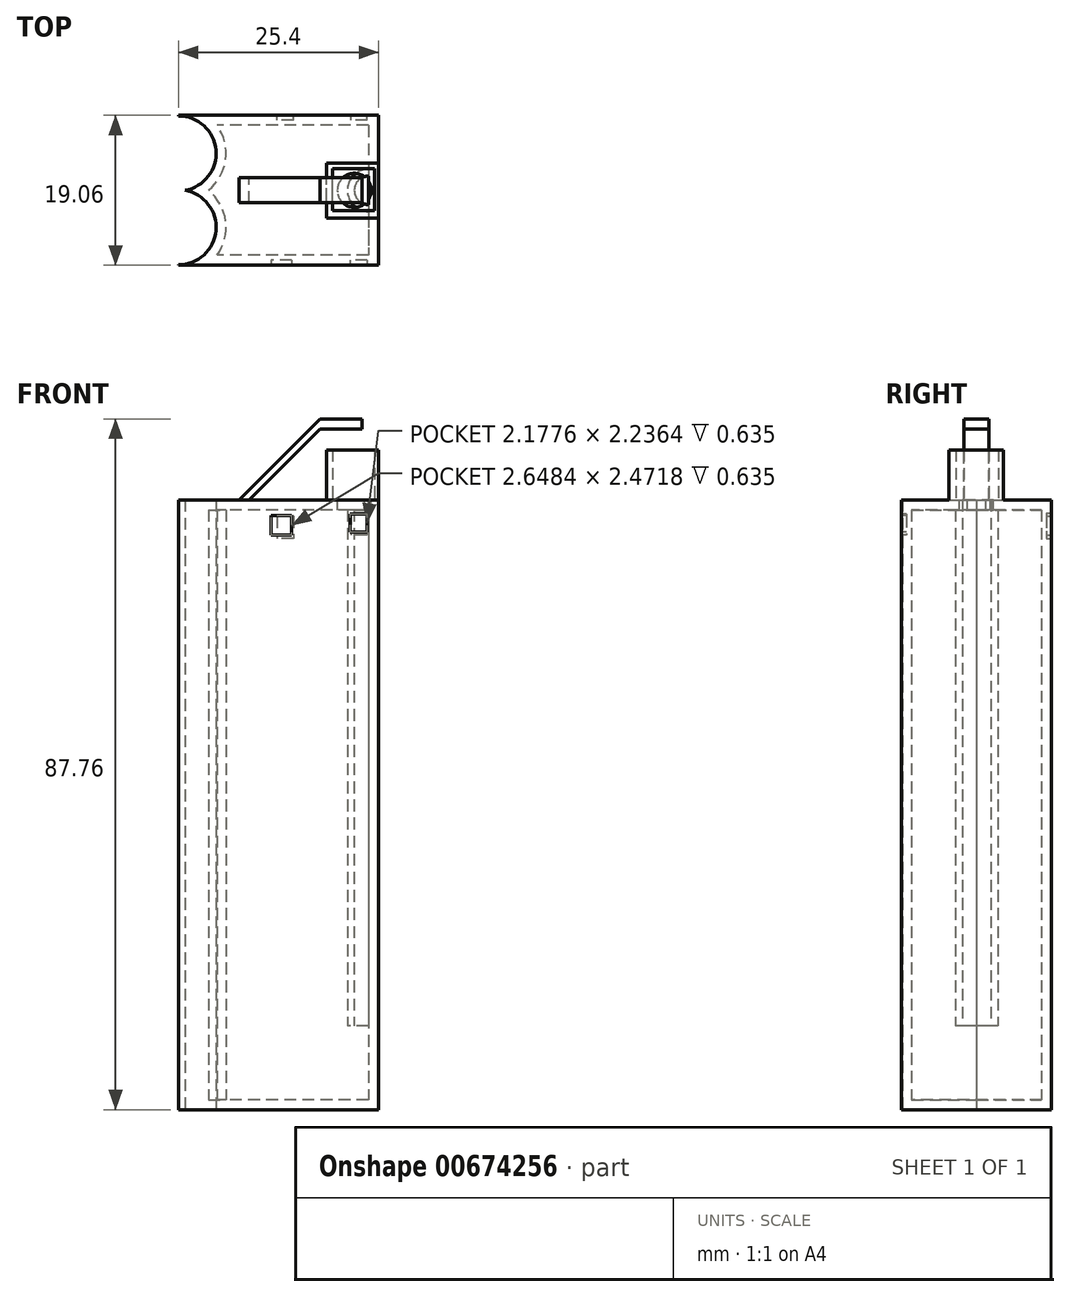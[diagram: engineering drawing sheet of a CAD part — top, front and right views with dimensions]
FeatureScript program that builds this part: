
annotation { "Feature Type Name" : "Feature", "Feature Type Description" : "" }
export const myFeature = defineFeature(function(context is Context, id is Id, definition is map)
    precondition{}
    {
        {
            var Q0;
            Q0=qCreatedBy(makeId("Top.planeOp"),FACE);
            var sketch = newSketch(context, id + "F0", { "sketchPlane" : qUnion([Q0])});
            skLineSegment(sketch, "E0.bottom", {"start": v(0, 9.53) * mm, "end": v(-25.4, 9.53) * mm});
            skLineSegment(sketch, "E0.top", {"start": v(0, -9.52) * mm, "end": v(-25.4, -9.53) * mm});
            skLineSegment(sketch, "E0.left", {"start": v(0, 9.53) * mm, "end": v(0, -9.52) * mm});
            skLineSegment(sketch, "E0.right", {"start": v(-25.4, 9.53) * mm, "end": v(-25.4, -9.53) * mm});
            skLineSegment(sketch, "E1", {"start": v(0, 0) * mm, "end": v(-25.4, 0) * mm, "construction": true});
            skCircle(sketch, "E2", {"center": v(-25.4, 4.7) * mm, "radius": 4.76 * mm});
            skCircle(sketch, "E3.MirrorC", {"center": v(-25.4, -4.7) * mm, "radius": 4.76 * mm});
            skSolve(sketch);
        }
        {
            var Q0;
            {var subQ1=sQuery(id+"F0.wireOp",EDGE,"E0.bottom");Q0=makeQuery(id+"F0.imprint","IMPRINT",FACE,{"disambiguationData":[TD([[makeQuery(id+"F0.imprint","IMPRINT",EDGE,{"derivedFrom":subQ1}),1.0]])]});}
            extrude(context, id + "F1", {"entities" : qUnion([Q0]), "depth" : 76.2 * mm, "offsetDistance" : 25.4 * mm});
        }
        {
            var Q0;
            Q0=makeQuery(id+"F1.opExtrude","CAP_FACE",FACE,{"disambiguationData":[OSD([sQuery(id+"F0.wireOp",EDGE,"E0.bottom"),sQuery(id+"F0.wireOp",EDGE,"E0.top"),sQuery(id+"F0.wireOp",EDGE,"E0.left"),sQuery(id+"F0.wireOp",EDGE,"E0.right"),sQuery(id+"F0.wireOp",EDGE,"E2"),sQuery(id+"F0.wireOp",EDGE,"E3.MirrorC")])],"isStart":false});
            shell(context, id + "F2", {"entities" : qUnion([Q0]), "thickness" : 1.27 * mm});
        }
        {
            var Q0;
            Q0=qCreatedBy(makeId("Top.planeOp"),FACE);
            var sketch = newSketch(context, id + "F3", { "sketchPlane" : qUnion([Q0])});
            skLineSegment(sketch, "E4.0", {"start": v(-1.27, 8.26) * mm, "end": v(-1.27, -8.25) * mm});
            skArc(sketch, "E5", {"start": v(-1.27, 1.81) * mm, "mid": v(-3.08, 0) * mm, "end": v(-1.27, -1.81) * mm});
            skArc(sketch, "E6", {"start": v(-1.27, 2.7) * mm, "mid": v(-3.96, 0) * mm, "end": v(-1.27, -2.7) * mm});
            skLineSegment(sketch, "E7", {"start": v(-1.27, 2.7) * mm, "end": v(-1.27, 1.81) * mm});
            skLineSegment(sketch, "E8", {"start": v(-1.27, -1.81) * mm, "end": v(-1.27, -2.7) * mm});
            skSolve(sketch);
        }
        {
            var Q0;
            Q0=makeQuery(id+"F3.imprint","IMPRINT",FACE,{"disambiguationData":[TD([[makeQuery(id+"F3.imprint","IMPRINT",EDGE,{"derivedFrom":sQuery(id+"F3.wireOp",EDGE,"E5")}),-1.0]])]});
            extrude(context, id + "F4", {"entities" : qUnion([Q0]), "operationType" : NewBodyOperationType.ADD, "depth" : 76.2 * mm, "offsetDistance" : 25.4 * mm});
        }
        {
            var Q0;
            {var subQ1=sQuery(id+"F0.wireOp",EDGE,"E0.top");var subQ5=sQuery(id+"F0.wireOp",EDGE,"E0.left");Q0=makeQuery(id+"F4.boolean.opBoolean","SPLIT",FACE,{"disambiguationData":[TD([makeQuery(id+"F2.opShell","OFFSET_FACE",FACE,{"disambiguationData":[OSD([subQ1])]})])],"derivedFrom":makeQuery(id+"F2.opShell","OFFSET_FACE",FACE,{"disambiguationData":[OSD([subQ5])]})});}
            var sketch = newSketch(context, id + "F5", { "sketchPlane" : qUnion([Q0])});
            skLineSegment(sketch, "E9.0", {"start": v(2.7, 1.27) * mm, "end": v(-2.7, 1.27) * mm});
            skLineSegment(sketch, "E10.bottom", {"start": v(-3.44, 1.27) * mm, "end": v(2.7, 1.27) * mm});
            skLineSegment(sketch, "E10.top", {"start": v(-3.44, 10.63) * mm, "end": v(2.7, 10.63) * mm});
            skLineSegment(sketch, "E10.left", {"start": v(-3.44, 1.27) * mm, "end": v(-3.44, 10.63) * mm});
            skLineSegment(sketch, "E10.right", {"start": v(2.7, 1.27) * mm, "end": v(2.7, 10.63) * mm});
            skSolve(sketch);
        }
        {
            var Q0;
            Q0=makeQuery(id+"F5.imprint","IMPRINT",FACE,{"disambiguationData":[TD([[makeQuery(id+"F5.imprint","IMPRINT",EDGE,{"derivedFrom":sQuery(id+"F5.wireOp",EDGE,"E10.top")}),-1.0]])]});
            extrude(context, id + "F6", {"entities" : qUnion([Q0]), "operationType" : NewBodyOperationType.REMOVE, "depth" : 12.7 * mm, "offsetDistance" : 25.4 * mm});
        }
        {
            var Q0;
            Q0=makeQuery(id+"F4.boolean.opBoolean","MERGE",FACE,{"derivedFrom":[makeQuery(id+"F1.opExtrude","CAP_FACE",FACE,{"disambiguationData":[OSD([sQuery(id+"F0.wireOp",EDGE,"E0.bottom"),sQuery(id+"F0.wireOp",EDGE,"E0.top"),sQuery(id+"F0.wireOp",EDGE,"E0.left"),sQuery(id+"F0.wireOp",EDGE,"E0.right"),sQuery(id+"F0.wireOp",EDGE,"E2"),sQuery(id+"F0.wireOp",EDGE,"E3.MirrorC")])],"isStart":false}),makeQuery(id+"F4.opExtrude","CAP_FACE",FACE,{"disambiguationData":[OSD([sQuery(id+"F3.wireOp",EDGE,"E5"),sQuery(id+"F3.wireOp",EDGE,"E6"),sQuery(id+"F3.wireOp",EDGE,"E7"),sQuery(id+"F3.wireOp",EDGE,"E8")])],"isStart":false})]});
            var sketch = newSketch(context, id + "F7", { "sketchPlane" : qUnion([Q0])});
            skLineSegment(sketch, "E11.0", {"start": v(0, 9.53) * mm, "end": v(-25.4, 9.53) * mm});
            skPoint(sketch, "E12.0", {"position": v(-1.27, 5.47) * mm});
            skLineSegment(sketch, "E13.0", {"start": v(0, 9.53) * mm, "end": v(0, -9.52) * mm});
            skLineSegment(sketch, "E14.0", {"start": v(0, -9.52) * mm, "end": v(-25.4, -9.53) * mm});
            skPoint(sketch, "E15.0", {"position": v(-20.66, -5.1) * mm});
            skArc(sketch, "E16.0", {"start": v(-24.58, 0) * mm, "mid": v(-20.66, -5.1) * mm, "end": v(-25.4, -9.45) * mm});
            skArc(sketch, "E17.0", {"start": v(-24.58, 0) * mm, "mid": v(-20.66, 5.1) * mm, "end": v(-25.4, 9.45) * mm});
            skArc(sketch, "E18.0", {"start": v(-1.27, 1.81) * mm, "mid": v(-3.08, 0) * mm, "end": v(-1.27, -1.81) * mm});
            skLineSegment(sketch, "E19.0", {"start": v(-1.27, 1.81) * mm, "end": v(-1.27, -1.81) * mm});
            skSolve(sketch);
        }
        {
            var Q0;
            Q0=makeQuery(id+"F7.imprint","IMPRINT",FACE,{"disambiguationData":[TD([[makeQuery(id+"F7.imprint","IMPRINT",EDGE,{"derivedFrom":sQuery(id+"F7.wireOp",EDGE,"E11.0")}),1.0]])]});
            var Q1;
            {var subQ4=sQuery(id+"F3.wireOp",EDGE,"E6");Q1=makeQuery(id+"F7.imprint","IMPRINT",FACE,{"disambiguationData":[TD([[makeQuery(id+"F7.imprint","IMPRINT",EDGE,{"derivedFrom":makeQuery(id+"F4.opExtrude","CAP_EDGE",EDGE,{"disambiguationData":[OSD([subQ4])],"isStart":false})}),-1.0]])]});}
            extrude(context, id + "F8", {"entities" : qUnion([Q0, Q1]), "operationType" : NewBodyOperationType.ADD, "depth" : 1.27 * mm, "offsetDistance" : 25.4 * mm});
        }
        {
            var Q0;
            Q0=makeQuery(id+"F8.opExtrude","CAP_FACE",FACE,{"disambiguationData":[OSD([sQuery(id+"F0.wireOp",EDGE,"E0.right"),sQuery(id+"F7.wireOp",EDGE,"E11.0"),sQuery(id+"F7.wireOp",EDGE,"E13.0"),sQuery(id+"F7.wireOp",EDGE,"E14.0"),sQuery(id+"F7.wireOp",EDGE,"E16.0"),sQuery(id+"F7.wireOp",EDGE,"E17.0"),sQuery(id+"F7.wireOp",EDGE,"E18.0"),sQuery(id+"F7.wireOp",EDGE,"E19.0")])],"isStart":false});
            var sketch = newSketch(context, id + "F9", { "sketchPlane" : qUnion([Q0])});
            skCircle(sketch, "E20", {"center": v(-3.08, 0) * mm, "radius": 2.16 * mm});
            skSolve(sketch);
        }
        {
            var Q0;
            {var subQ0=sQuery(id+"F9.wireOp",EDGE,"E20");var subQ1=makeQuery(id+"F8.opExtrude","CAP_EDGE",EDGE,{"disambiguationData":[OSD([sQuery(id+"F7.wireOp",EDGE,"E18.0")])],"isStart":false});var subQ2=makeQuery(id+"F9.imprint","INTERSECT",VERTEX,{"disambiguationData":[OD(0.0)],"derivedFrom":[subQ1,subQ0]});Q0=makeQuery(id+"F9.imprint","IMPRINT",FACE,{"disambiguationData":[TD([[makeQuery(id+"F9.imprint","IMPRINT",EDGE,{"disambiguationData":[TD([[subQ2,-1.0]])],"derivedFrom":subQ0}),1.0]])]});}
            var Q1;
            {var subQ0=sQuery(id+"F9.wireOp",EDGE,"E20");var subQ1=makeQuery(id+"F8.opExtrude","CAP_EDGE",EDGE,{"disambiguationData":[OSD([sQuery(id+"F7.wireOp",EDGE,"E19.0")])],"isStart":false});var subQ2=makeQuery(id+"F9.imprint","INTERSECT",VERTEX,{"disambiguationData":[OD(0.0)],"derivedFrom":[subQ1,subQ0]});Q1=makeQuery(id+"F9.imprint","IMPRINT",FACE,{"disambiguationData":[TD([[makeQuery(id+"F9.imprint","IMPRINT",EDGE,{"disambiguationData":[TD([[subQ2,1.0]])],"derivedFrom":subQ0}),1.0]])]});}
            var Q2;
            {var subQ0=sQuery(id+"F9.wireOp",EDGE,"E20");var subQ1=makeQuery(id+"F8.opExtrude","CAP_EDGE",EDGE,{"disambiguationData":[OSD([sQuery(id+"F7.wireOp",EDGE,"E18.0")])],"isStart":false});var subQ2=makeQuery(id+"F9.imprint","INTERSECT",VERTEX,{"disambiguationData":[OD(0.0)],"derivedFrom":[subQ1,subQ0]});Q2=makeQuery(id+"F9.imprint","IMPRINT",FACE,{"disambiguationData":[TD([[makeQuery(id+"F9.imprint","IMPRINT",EDGE,{"disambiguationData":[TD([[subQ2,1.0]])],"derivedFrom":subQ0}),1.0]])]});}
            extrude(context, id + "F10", {"entities" : qUnion([Q0, Q1, Q2]), "operationType" : NewBodyOperationType.REMOVE, "oppositeDirection" : true, "depth" : 1.27 * mm, "offsetDistance" : 25.4 * mm});
        }
        {
            var Q0;
            Q0=qCreatedBy(makeId("Front.planeOp"),FACE);
            var sketch = newSketch(context, id + "F11", { "sketchPlane" : qUnion([Q0])});
            skLineSegment(sketch, "E21.0", {"start": v(0, 77.47) * mm, "end": v(-25.4, 77.47) * mm, "construction": true});
            skLineSegment(sketch, "E22", {"start": v(-17.73, 77.47) * mm, "end": v(-7.44, 87.76) * mm});
            skLineSegment(sketch, "E23", {"start": v(-7.44, 87.76) * mm, "end": v(-2.11, 87.76) * mm});
            skLineSegment(sketch, "E24", {"start": v(-2.11, 86.49) * mm, "end": v(-7.44, 86.49) * mm});
            skLineSegment(sketch, "E25", {"start": v(-7.44, 86.49) * mm, "end": v(-16.46, 77.47) * mm});
            skLineSegment(sketch, "E26", {"start": v(-2.11, 87.76) * mm, "end": v(-2.11, 86.49) * mm});
            skLineSegment(sketch, "E27", {"start": v(-16.46, 77.47) * mm, "end": v(-17.73, 77.47) * mm});
            skSolve(sketch);
        }
        {
            var Q0;
            Q0=makeQuery(id+"F11.imprint","IMPRINT",FACE,{"disambiguationData":[TD([[makeQuery(id+"F11.imprint","IMPRINT",EDGE,{"derivedFrom":sQuery(id+"F11.wireOp",EDGE,"jf9fpn2J-BByt-Q0SO-4Lyf-H6Ji1VYWbdJu")}),1.0]])]});
            var Q1;
            Q1=makeQuery(id+"F11.imprint","IMPRINT",FACE,{"disambiguationData":[TD([[makeQuery(id+"F11.imprint","IMPRINT",EDGE,{"derivedFrom":sQuery(id+"F11.wireOp",EDGE,"E22")}),-1.0]])]});
            extrude(context, id + "F12", {"entities" : qUnion([Q0, Q1]), "operationType" : NewBodyOperationType.ADD, "depth" : 3.17 * mm, "offsetDistance" : 25.4 * mm, "symmetric" : true});
        }
        {
            var Q0;
            Q0=makeQuery(id+"F8.opExtrude","CAP_FACE",FACE,{"disambiguationData":[OSD([sQuery(id+"F0.wireOp",EDGE,"E0.right"),sQuery(id+"F7.wireOp",EDGE,"E11.0"),sQuery(id+"F7.wireOp",EDGE,"E13.0"),sQuery(id+"F7.wireOp",EDGE,"E14.0"),sQuery(id+"F7.wireOp",EDGE,"E16.0"),sQuery(id+"F7.wireOp",EDGE,"E17.0"),sQuery(id+"F7.wireOp",EDGE,"E18.0"),sQuery(id+"F7.wireOp",EDGE,"E19.0")])],"isStart":false});
            var sketch = newSketch(context, id + "F13", { "sketchPlane" : qUnion([Q0])});
            skLineSegment(sketch, "E28.bottom", {"start": v(0, -3.52) * mm, "end": v(-6.6, -3.52) * mm});
            skLineSegment(sketch, "E28.top", {"start": v(0, 3.43) * mm, "end": v(-6.6, 3.43) * mm});
            skLineSegment(sketch, "E28.left", {"start": v(0, -3.52) * mm, "end": v(0, 3.43) * mm});
            skLineSegment(sketch, "E28.right", {"start": v(-6.6, -3.52) * mm, "end": v(-6.6, 3.43) * mm});
            skLineSegment(sketch, "E29.bottom", {"start": v(-0.53, -2.6) * mm, "end": v(-5.85, -2.6) * mm});
            skLineSegment(sketch, "E29.top", {"start": v(-0.53, 2.77) * mm, "end": v(-5.85, 2.77) * mm});
            skLineSegment(sketch, "E29.left", {"start": v(-0.53, -2.6) * mm, "end": v(-0.53, 2.77) * mm});
            skLineSegment(sketch, "E29.right", {"start": v(-5.85, -2.6) * mm, "end": v(-5.85, 2.77) * mm});
            skSolve(sketch);
        }
        {
            var Q0;
            Q0=makeQuery(id+"F13.imprint","IMPRINT",FACE,{"disambiguationData":[TD([[makeQuery(id+"F13.imprint","IMPRINT",EDGE,{"derivedFrom":sQuery(id+"F13.wireOp",EDGE,"E28.bottom")}),-1.0]])]});
            extrude(context, id + "F14", {"entities" : qUnion([Q0]), "operationType" : NewBodyOperationType.ADD, "depth" : 6.35 * mm, "offsetDistance" : 25.4 * mm});
        }
        {
            var Q0;
            Q0=makeQuery(id+"F8.boolean.opBoolean","MERGE",FACE,{"derivedFrom":[makeQuery(id+"F1.opExtrude","SWEPT_FACE",FACE,{"disambiguationData":[OSD([sQuery(id+"F0.wireOp",EDGE,"E0.bottom")])]}),makeQuery(id+"F8.opExtrude","SWEPT_FACE",FACE,{"disambiguationData":[OSD([sQuery(id+"F7.wireOp",EDGE,"E11.0")])]})]});
            var sketch = newSketch(context, id + "F15", { "sketchPlane" : qUnion([Q0])});
            skLineSegment(sketch, "E30.bottom", {"start": v(1.45, 75.8) * mm, "end": v(3.5, 75.8) * mm});
            skLineSegment(sketch, "E30.top", {"start": v(1.45, 72.97) * mm, "end": v(3.5, 72.97) * mm});
            skLineSegment(sketch, "E30.left", {"start": v(1.45, 75.8) * mm, "end": v(1.45, 72.97) * mm});
            skLineSegment(sketch, "E30.right", {"start": v(3.5, 75.8) * mm, "end": v(3.5, 72.97) * mm});
            skLineSegment(sketch, "E31.bottom", {"start": v(10.8, 75.4) * mm, "end": v(12.92, 75.4) * mm});
            skLineSegment(sketch, "E31.top", {"start": v(10.8, 72.58) * mm, "end": v(12.92, 72.58) * mm});
            skLineSegment(sketch, "E31.left", {"start": v(10.8, 75.4) * mm, "end": v(10.8, 72.58) * mm});
            skLineSegment(sketch, "E31.right", {"start": v(12.92, 75.4) * mm, "end": v(12.92, 72.58) * mm});
            skSolve(sketch);
        }
        {
            var Q0;
            Q0=makeQuery(id+"F15.imprint","IMPRINT",FACE,{"disambiguationData":[TD([[makeQuery(id+"F15.imprint","IMPRINT",EDGE,{"derivedFrom":sQuery(id+"F15.wireOp",EDGE,"E30.bottom")}),-1.0]])]});
            var Q1;
            Q1=makeQuery(id+"F15.imprint","IMPRINT",FACE,{"disambiguationData":[TD([[makeQuery(id+"F15.imprint","IMPRINT",EDGE,{"derivedFrom":sQuery(id+"F15.wireOp",EDGE,"E31.bottom")}),-1.0]])]});
            extrude(context, id + "F16", {"entities" : qUnion([Q0, Q1]), "operationType" : NewBodyOperationType.REMOVE, "oppositeDirection" : true, "depth" : 0.64 * mm, "offsetDistance" : 25.4 * mm});
        }
        {
            var Q0;
            Q0=makeQuery(id+"F8.boolean.opBoolean","MERGE",FACE,{"derivedFrom":[makeQuery(id+"F1.opExtrude","SWEPT_FACE",FACE,{"disambiguationData":[OSD([sQuery(id+"F0.wireOp",EDGE,"E0.top")])]}),makeQuery(id+"F8.opExtrude","SWEPT_FACE",FACE,{"disambiguationData":[OSD([sQuery(id+"F7.wireOp",EDGE,"E14.0")])]})]});
            var sketch = newSketch(context, id + "F17", { "sketchPlane" : qUnion([Q0])});
            skLineSegment(sketch, "E32.bottom", {"start": v(-1.43, 75.64) * mm, "end": v(-3.61, 75.64) * mm});
            skLineSegment(sketch, "E32.top", {"start": v(-1.43, 73.4) * mm, "end": v(-3.61, 73.4) * mm});
            skLineSegment(sketch, "E32.left", {"start": v(-1.43, 75.64) * mm, "end": v(-1.43, 73.4) * mm});
            skLineSegment(sketch, "E32.right", {"start": v(-3.61, 75.64) * mm, "end": v(-3.61, 73.4) * mm});
            skLineSegment(sketch, "E33.bottom", {"start": v(-11.03, 75.47) * mm, "end": v(-13.68, 75.47) * mm});
            skLineSegment(sketch, "E33.top", {"start": v(-11.03, 73) * mm, "end": v(-13.68, 73) * mm});
            skLineSegment(sketch, "E33.left", {"start": v(-11.03, 75.47) * mm, "end": v(-11.03, 73) * mm});
            skLineSegment(sketch, "E33.right", {"start": v(-13.68, 75.47) * mm, "end": v(-13.68, 73) * mm});
            skSolve(sketch);
        }
        {
            var Q0;
            Q0=makeQuery(id+"F17.imprint","IMPRINT",FACE,{"disambiguationData":[TD([[makeQuery(id+"F17.imprint","IMPRINT",EDGE,{"derivedFrom":sQuery(id+"F17.wireOp",EDGE,"E33.bottom")}),1.0]])]});
            var Q1;
            Q1=makeQuery(id+"F17.imprint","IMPRINT",FACE,{"disambiguationData":[TD([[makeQuery(id+"F17.imprint","IMPRINT",EDGE,{"derivedFrom":sQuery(id+"F17.wireOp",EDGE,"E32.bottom")}),1.0]])]});
            extrude(context, id + "F18", {"entities" : qUnion([Q0, Q1]), "operationType" : NewBodyOperationType.REMOVE, "oppositeDirection" : true, "depth" : 0.64 * mm, "offsetDistance" : 25.4 * mm});
        }
    });
